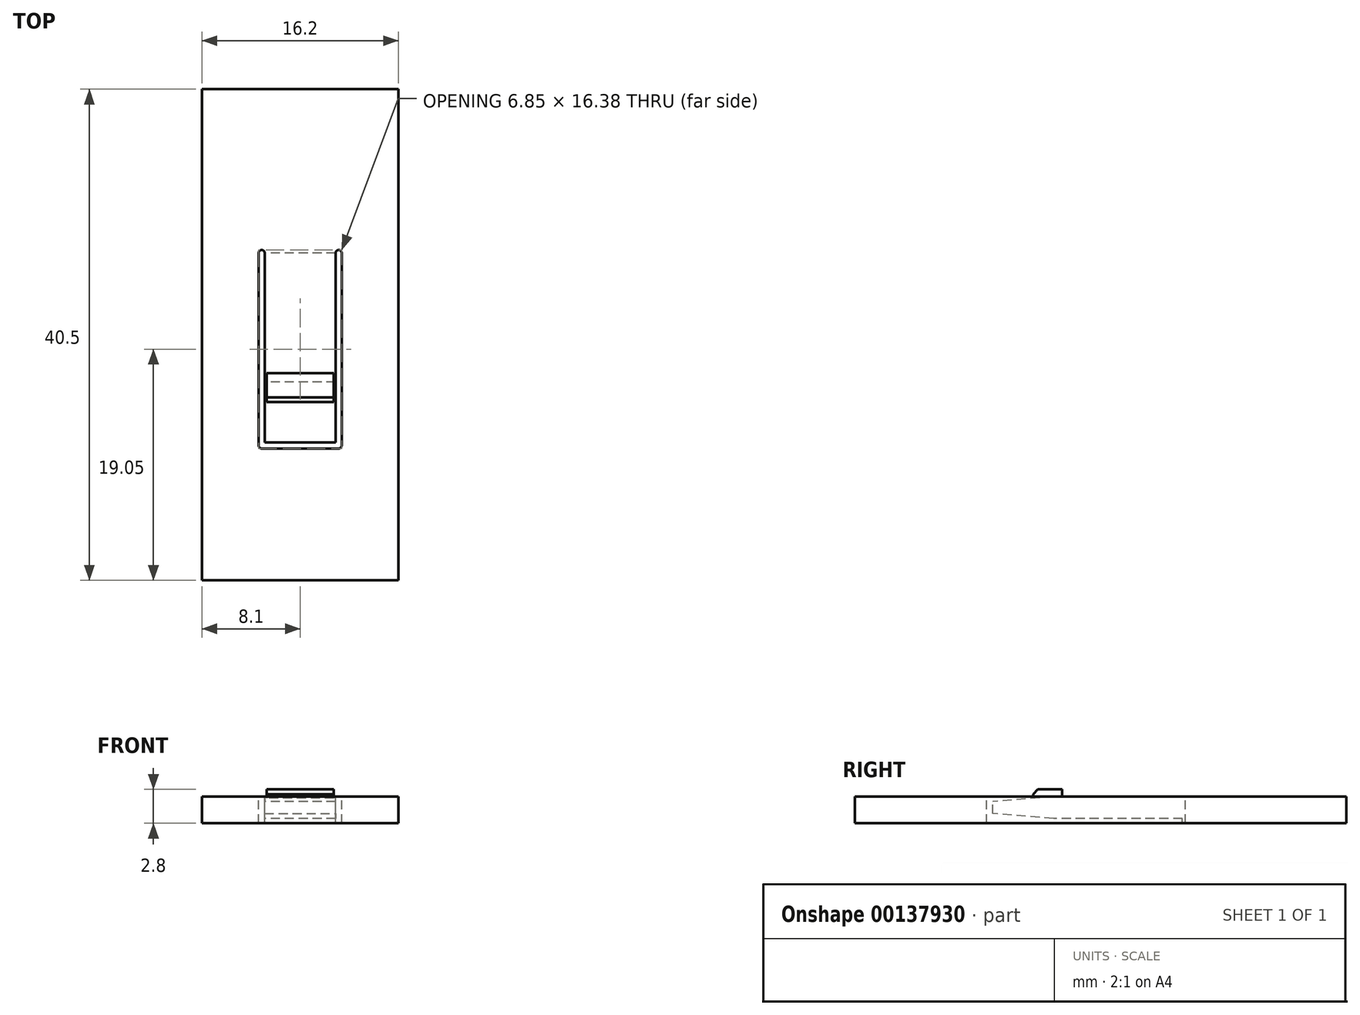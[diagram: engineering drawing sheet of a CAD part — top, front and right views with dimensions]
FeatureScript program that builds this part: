
annotation { "Feature Type Name" : "Feature", "Feature Type Description" : "" }
export const myFeature = defineFeature(function(context is Context, id is Id, definition is map)
    precondition{}
    {
        {
            var Q0;
            Q0=qCreatedBy(makeId("Top.planeOp"),FACE);
            var sketch = newSketch(context, id + "F0", { "sketchPlane" : qUnion([Q0])});
            skLineSegment(sketch, "E0.bottom", {"start": v(0, 0) * mm, "end": v(16.2, 0) * mm});
            skLineSegment(sketch, "E0.top", {"start": v(0, 40.5) * mm, "end": v(16.2, 40.5) * mm});
            skLineSegment(sketch, "E0.left", {"start": v(0, 0) * mm, "end": v(0, 40.5) * mm});
            skLineSegment(sketch, "E0.right", {"start": v(16.2, 0) * mm, "end": v(16.2, 40.5) * mm});
            skLineSegment(sketch, "E1.bottom", {"start": v(11.28, 17.46) * mm, "end": v(4.92, 17.46) * mm, "construction": true});
            skLineSegment(sketch, "E1.top", {"start": v(11.28, 14.29) * mm, "end": v(4.92, 14.29) * mm, "construction": true});
            skLineSegment(sketch, "E1.left", {"start": v(11.28, 17.46) * mm, "end": v(11.28, 14.29) * mm, "construction": true});
            skLineSegment(sketch, "E1.right", {"start": v(4.92, 17.46) * mm, "end": v(4.92, 14.29) * mm, "construction": true});
            skPoint(sketch, "E1.middle", {"position": v(8.1, 15.88) * mm});
            skPoint(sketch, "E1.middle.positionSnap0", {"position": v(8.1, 0) * mm});
            skPoint(sketch, "E1.centerSnap0", {"position": v(8.1, 0) * mm});
            skLineSegment(sketch, "E2", {"start": v(4.92, 26.99) * mm, "end": v(4.92, 11.11) * mm, "construction": true});
            skLineSegment(sketch, "E3", {"start": v(4.92, 11.11) * mm, "end": v(11.28, 11.11) * mm, "construction": true});
            skLineSegment(sketch, "E4", {"start": v(11.28, 11.11) * mm, "end": v(11.28, 26.99) * mm, "construction": true});
            skArc(sketch, "E5.0.startCap", {"start": v(4.92, 10.86) * mm, "mid": v(4.67, 11.11) * mm, "end": v(4.92, 11.36) * mm});
            skArc(sketch, "E5.0.endCap", {"start": v(11.28, 11.36) * mm, "mid": v(11.53, 11.11) * mm, "end": v(11.28, 10.86) * mm});
            skLineSegment(sketch, "E5.0.left", {"start": v(4.92, 11.36) * mm, "end": v(11.28, 11.36) * mm});
            skLineSegment(sketch, "E5.0.right", {"start": v(4.92, 10.86) * mm, "end": v(11.28, 10.86) * mm});
            skArc(sketch, "E5.1.startCap", {"start": v(4.67, 26.99) * mm, "mid": v(4.92, 27.24) * mm, "end": v(5.17, 26.99) * mm});
            skArc(sketch, "E5.1.endCap", {"start": v(5.17, 11.11) * mm, "mid": v(4.92, 10.86) * mm, "end": v(4.67, 11.11) * mm});
            skLineSegment(sketch, "E5.1.left", {"start": v(5.17, 26.99) * mm, "end": v(5.17, 11.11) * mm});
            skLineSegment(sketch, "E5.1.right", {"start": v(4.67, 26.99) * mm, "end": v(4.67, 11.11) * mm});
            skArc(sketch, "E5.2.startCap", {"start": v(11.53, 11.11) * mm, "mid": v(11.28, 10.86) * mm, "end": v(11.03, 11.11) * mm});
            skArc(sketch, "E5.2.endCap", {"start": v(11.03, 26.99) * mm, "mid": v(11.28, 27.24) * mm, "end": v(11.53, 26.99) * mm});
            skLineSegment(sketch, "E5.2.left", {"start": v(11.03, 11.11) * mm, "end": v(11.03, 26.99) * mm});
            skLineSegment(sketch, "E5.2.right", {"start": v(11.53, 11.11) * mm, "end": v(11.53, 26.99) * mm});
            skLineSegment(sketch, "E6.0", {"start": v(10.88, 14.69) * mm, "end": v(5.32, 14.69) * mm});
            skLineSegment(sketch, "E6.1", {"start": v(10.88, 17.06) * mm, "end": v(10.88, 14.69) * mm});
            skLineSegment(sketch, "E6.2", {"start": v(10.88, 17.06) * mm, "end": v(5.32, 17.06) * mm});
            skLineSegment(sketch, "E6.3", {"start": v(5.32, 17.06) * mm, "end": v(5.32, 14.69) * mm});
            skLineSegment(sketch, "E7", {"start": v(11.28, 26.99) * mm, "end": v(4.92, 26.99) * mm});
            skSolve(sketch);
        }
        {
            var Q0;
            Q0=makeQuery(id+"F0.imprint","IMPRINT",FACE,{"disambiguationData":[TD([[makeQuery(id+"F0.imprint","IMPRINT",EDGE,{"derivedFrom":sQuery(id+"F0.wireOp",EDGE,"E0.bottom")}),1.0]])]});
            extrude(context, id + "F1", {"entities" : qUnion([Q0]), "oppositeDirection" : true, "depth" : 2.2 * mm});
        }
        {
            var Q0;
            Q0=makeQuery(id+"F0.imprint","IMPRINT",FACE,{"disambiguationData":[TD([[makeQuery(id+"F0.imprint","IMPRINT",EDGE,{"derivedFrom":sQuery(id+"F0.wireOp",EDGE,"E6.0")}),-1.0]])]});
            var Q1;
            Q1=makeQuery(id+"F0.imprint","IMPRINT",FACE,{"disambiguationData":[TD([[makeQuery(id+"F0.imprint","IMPRINT",EDGE,{"derivedFrom":sQuery(id+"F0.wireOp",EDGE,"E6.0")}),1.0]])]});
            extrude(context, id + "F2", {"entities" : qUnion([Q0, Q1]), "operationType" : NewBodyOperationType.ADD, "oppositeDirection" : true, "depth" : 1.8 * mm});
        }
        {
            var Q0;
            Q0=makeQuery(id+"F0.imprint","IMPRINT",FACE,{"disambiguationData":[TD([[makeQuery(id+"F0.imprint","IMPRINT",EDGE,{"derivedFrom":sQuery(id+"F0.wireOp",EDGE,"E6.0")}),-1.0]])]});
            extrude(context, id + "F3", {"entities" : qUnion([Q0]), "operationType" : NewBodyOperationType.ADD, "depth" : .6 * mm});
        }
        {
            var Q0;
            Q0=makeQuery(id+"F2.opExtrude","CAP_EDGE",EDGE,{"disambiguationData":[OSD([sQuery(id+"F0.wireOp",EDGE,"E5.0.left")])],"isStart":true});
            var Q1;
            Q1=makeQuery(id+"F2.opExtrude","CAP_EDGE",EDGE,{"disambiguationData":[OSD([sQuery(id+"F0.wireOp",EDGE,"E5.0.left")])],"isStart":false});
            chamfer(context, id + "F4", {"entities" : qUnion([Q0, Q1]), "chamferType" : ChamferType.TWO_OFFSETS, "width1" : 5 * mm, "oppositeDirection" : false, "width2" : .4 * mm, "tangentPropagation" : true});
        }
        {
            var Q0;
            Q0=makeQuery(id+"F3.opExtrude","CAP_EDGE",EDGE,{"disambiguationData":[OSD([sQuery(id+"F0.wireOp",EDGE,"E6.0")])],"isStart":false});
            var Q1;
            Q1=makeQuery(id+"F2.opExtrude","CAP_EDGE",EDGE,{"disambiguationData":[OSD([sQuery(id+"F0.wireOp",EDGE,"E7")])],"isStart":false});
            chamfer(context, id + "F5", {"entities" : qUnion([Q0, Q1]), "width" : .4 * mm, "tangentPropagation" : true});
        }
    });
